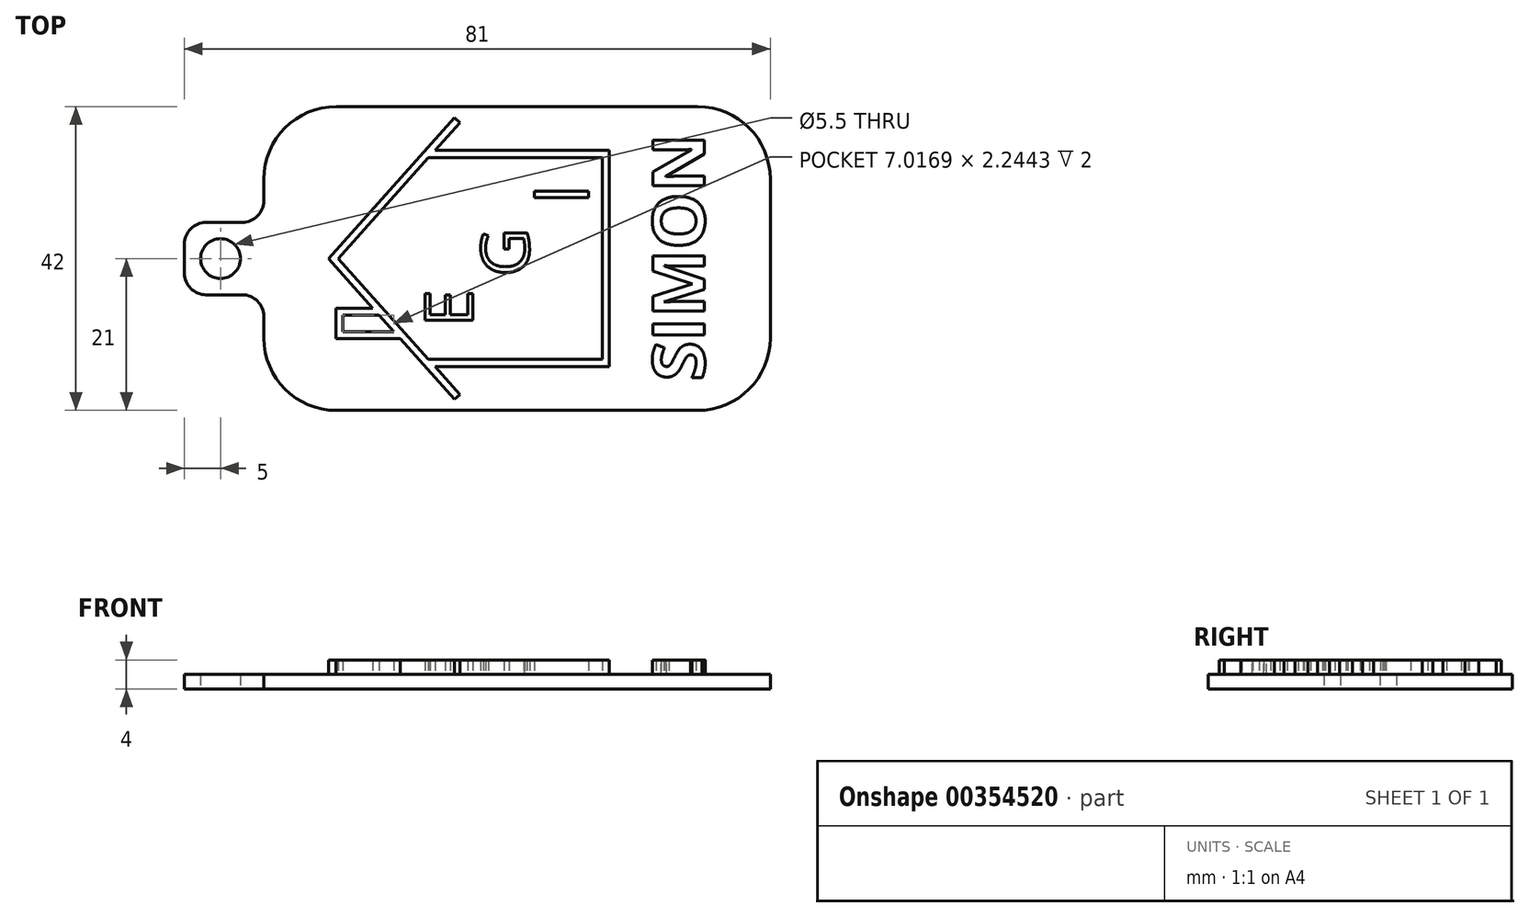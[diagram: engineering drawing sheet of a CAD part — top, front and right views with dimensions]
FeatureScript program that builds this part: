
annotation { "Feature Type Name" : "Feature", "Feature Type Description" : "" }
export const myFeature = defineFeature(function(context is Context, id is Id, definition is map)
    precondition{}
    {
        {
            var Q0;
            Q0=qCreatedBy(makeId("Top.planeOp"),FACE);
            var sketch = newSketch(context, id + "F0", { "sketchPlane" : qUnion([Q0])});
            skLineSegment(sketch, "E0.bottom", {"start": v(30, 21) * mm, "end": v(-20, 21) * mm});
            skLineSegment(sketch, "E0.top", {"start": v(30, -21) * mm, "end": v(-20, -21) * mm});
            skLineSegment(sketch, "E0.left", {"start": v(40, 11) * mm, "end": v(40, -11) * mm});
            skLineSegment(sketch, "E0.right", {"start": v(-30, 11) * mm, "end": v(-30, 8) * mm});
            skLineSegment(sketch, "E1.bottom", {"start": v(-38, 5) * mm, "end": v(-33, 5) * mm});
            skLineSegment(sketch, "E1.top", {"start": v(-38, -5) * mm, "end": v(-33, -5) * mm});
            skLineSegment(sketch, "E1.left", {"start": v(-41, 2) * mm, "end": v(-41, -2) * mm});
            skLineSegment(sketch, "E2.trimOffspring", {"start": v(-30, -8) * mm, "end": v(-30, -11) * mm});
            skPoint(sketch, "E3.visualSharp", {"position": v(-30, 5) * mm});
            skArc(sketch, "E3.filletArc", {"start": v(-33, 5) * mm, "mid": v(-30.88, 5.88) * mm, "end": v(-30, 8) * mm});
            skPoint(sketch, "E4.visualSharp", {"position": v(-41, 5) * mm});
            skArc(sketch, "E4.filletArc", {"start": v(-38, 5) * mm, "mid": v(-40.12, 4.12) * mm, "end": v(-41, 2) * mm});
            skPoint(sketch, "E5.visualSharp", {"position": v(-41, -5) * mm});
            skArc(sketch, "E5.filletArc", {"start": v(-41, -2) * mm, "mid": v(-40.12, -4.12) * mm, "end": v(-38, -5) * mm});
            skPoint(sketch, "E6.visualSharp", {"position": v(-30, -5) * mm});
            skArc(sketch, "E6.filletArc", {"start": v(-30, -8) * mm, "mid": v(-30.88, -5.88) * mm, "end": v(-33, -5) * mm});
            skPoint(sketch, "E7.visualSharp", {"position": v(-30, 21) * mm});
            skArc(sketch, "E7.filletArc", {"start": v(-20, 21) * mm, "mid": v(-27.07, 18.07) * mm, "end": v(-30, 11) * mm});
            skPoint(sketch, "E8.visualSharp", {"position": v(-30, -21) * mm});
            skArc(sketch, "E8.filletArc", {"start": v(-30, -11) * mm, "mid": v(-27.07, -18.07) * mm, "end": v(-20, -21) * mm});
            skPoint(sketch, "E9.visualSharp", {"position": v(40, 21) * mm});
            skArc(sketch, "E9.filletArc", {"start": v(40, 11) * mm, "mid": v(37.07, 18.07) * mm, "end": v(30, 21) * mm});
            skPoint(sketch, "E10.visualSharp", {"position": v(40, -21) * mm});
            skArc(sketch, "E10.filletArc", {"start": v(30, -21) * mm, "mid": v(37.07, -18.07) * mm, "end": v(40, -11) * mm});
            skCircle(sketch, "E11", {"center": v(-36, 0) * mm, "radius": 2.75 * mm});
            skPoint(sketch, "E11.centerSnap0", {"position": v(-41, 0) * mm});
            skSolve(sketch);
        }
        {
            var Q0;
            Q0=makeQuery(id+"F0.imprint","IMPRINT",FACE,{"disambiguationData":[TD([[makeQuery(id+"F0.imprint","IMPRINT",EDGE,{"derivedFrom":sQuery(id+"F0.wireOp",EDGE,"E0.bottom")}),1.0]])]});
            extrude(context, id + "F1", {"entities" : qUnion([Q0]), "depth" : 2 * mm});
        }
        {
            var Q0;
            Q0=makeQuery(id+"F1.opExtrude","CAP_FACE",FACE,{"disambiguationData":[OSD([sQuery(id+"F0.wireOp",EDGE,"E0.bottom"),sQuery(id+"F0.wireOp",EDGE,"E0.top"),sQuery(id+"F0.wireOp",EDGE,"E0.left"),sQuery(id+"F0.wireOp",EDGE,"E0.right"),sQuery(id+"F0.wireOp",EDGE,"E1.bottom"),sQuery(id+"F0.wireOp",EDGE,"E1.top"),sQuery(id+"F0.wireOp",EDGE,"E1.left"),sQuery(id+"F0.wireOp",EDGE,"E2.trimOffspring"),sQuery(id+"F0.wireOp",EDGE,"E3.filletArc"),sQuery(id+"F0.wireOp",EDGE,"E4.filletArc"),sQuery(id+"F0.wireOp",EDGE,"E5.filletArc"),sQuery(id+"F0.wireOp",EDGE,"E6.filletArc"),sQuery(id+"F0.wireOp",EDGE,"E7.filletArc"),sQuery(id+"F0.wireOp",EDGE,"E8.filletArc"),sQuery(id+"F0.wireOp",EDGE,"E9.filletArc"),sQuery(id+"F0.wireOp",EDGE,"E10.filletArc"),sQuery(id+"F0.wireOp",EDGE,"E11")])],"isStart":false});
            var sketch = newSketch(context, id + "F2", { "sketchPlane" : qUnion([Q0])});
            skLineSegment(sketch, "E12", {"start": v(-19.74, 0) * mm, "end": v(-7.25, -13.94) * mm});
            skLineSegment(sketch, "E13", {"start": v(-6.35, -14.94) * mm, "end": v(17.76, -14.94) * mm});
            skLineSegment(sketch, "E14", {"start": v(16.76, -13.94) * mm, "end": v(16.76, 0) * mm});
            skLineSegment(sketch, "E15.0", {"start": v(-21.08, 0) * mm, "end": v(-14.95, -6.84) * mm});
            skLineSegment(sketch, "E16.0", {"start": v(-7.25, -13.94) * mm, "end": v(16.76, -13.94) * mm});
            skLineSegment(sketch, "E17.0", {"start": v(17.76, -14.94) * mm, "end": v(17.76, 0) * mm});
            skLineSegment(sketch, "E18", {"start": v(-3.64, -19.47) * mm, "end": v(-2.9, -18.8) * mm});
            skLineSegment(sketch, "E19.trimOffspring", {"start": v(-6.35, -14.94) * mm, "end": v(-2.9, -18.8) * mm});
            skLineSegment(sketch, "E20", {"start": v(-14.06, -7.84) * mm, "end": v(-19.06, -7.84) * mm});
            skLineSegment(sketch, "E21.0", {"start": v(-11.15, -11.09) * mm, "end": v(-20.06, -11.09) * mm});
            skLineSegment(sketch, "E22.0", {"start": v(-46, 2) * mm, "end": v(-46, -2) * mm});
            skArc(sketch, "E22.1", {"start": v(-38, 10) * mm, "mid": v(-43.66, 7.66) * mm, "end": v(-46, 2) * mm});
            skLineSegment(sketch, "E22.2", {"start": v(-35, 10) * mm, "end": v(-38, 10) * mm});
            skLineSegment(sketch, "E22.3", {"start": v(-20, -26) * mm, "end": v(30, -26) * mm});
            skArc(sketch, "E22.4", {"start": v(-35, -11) * mm, "mid": v(-30.6, -21.6) * mm, "end": v(-20, -26) * mm});
            skLineSegment(sketch, "E22.5", {"start": v(-35, -10) * mm, "end": v(-35, -11) * mm});
            skLineSegment(sketch, "E22.6", {"start": v(-38, -10) * mm, "end": v(-35, -10) * mm});
            skArc(sketch, "E22.7", {"start": v(30, -26) * mm, "mid": v(40.6, -21.6) * mm, "end": v(45, -11) * mm});
            skLineSegment(sketch, "E22.8", {"start": v(45, -11) * mm, "end": v(45, 11) * mm});
            skArc(sketch, "E22.9", {"start": v(45, 11) * mm, "mid": v(40.6, 21.6) * mm, "end": v(30, 26) * mm});
            skArc(sketch, "E22.10", {"start": v(-46, -2) * mm, "mid": v(-43.66, -7.66) * mm, "end": v(-38, -10) * mm});
            skLineSegment(sketch, "E22.11", {"start": v(30, 26) * mm, "end": v(-20, 26) * mm});
            skArc(sketch, "E22.12", {"start": v(-20, 26) * mm, "mid": v(-30.6, 21.6) * mm, "end": v(-35, 11) * mm});
            skLineSegment(sketch, "E22.13", {"start": v(-35, 11) * mm, "end": v(-35, 10) * mm});
            skLineSegment(sketch, "E23", {"start": v(-19.06, -10.09) * mm, "end": v(-19.06, -7.84) * mm});
            skLineSegment(sketch, "E24.0", {"start": v(-20.06, -11.09) * mm, "end": v(-20.06, -6.84) * mm});
            skLineSegment(sketch, "E25.trimOffspring", {"start": v(-11.15, -11.09) * mm, "end": v(-3.64, -19.47) * mm});
            skLineSegment(sketch, "E26.trimOffspring", {"start": v(-12.04, -10.09) * mm, "end": v(-19.06, -10.09) * mm});
            skLineSegment(sketch, "E27.trimOffspring", {"start": v(-14.95, -6.84) * mm, "end": v(-20.06, -6.84) * mm});
            skLineSegment(sketch, "E28.trimOffspring", {"start": v(-14.06, -7.84) * mm, "end": v(-12.04, -10.09) * mm});
            skLineSegment(sketch, "E29", {"start": v(0, 0) * mm, "end": v(-30, 0) * mm, "construction": true});
            skLineSegment(sketch, "E30.MirrorCS", {"start": v(16.76, 13.94) * mm, "end": v(16.76, 0) * mm});
            skLineSegment(sketch, "E31.MirrorCS", {"start": v(17.76, 14.94) * mm, "end": v(17.76, 0) * mm});
            skLineSegment(sketch, "E32.MirrorCS", {"start": v(-6.35, 14.94) * mm, "end": v(17.76, 14.94) * mm});
            skLineSegment(sketch, "E33.MirrorCS", {"start": v(-7.25, 13.94) * mm, "end": v(16.76, 13.94) * mm});
            skLineSegment(sketch, "E34.MirrorCS", {"start": v(-6.35, 14.94) * mm, "end": v(-2.9, 18.8) * mm});
            skLineSegment(sketch, "E35.MirrorCS", {"start": v(-21.08, 0) * mm, "end": v(-3.64, 19.47) * mm});
            skLineSegment(sketch, "E36.MirrorCS", {"start": v(-3.64, 19.47) * mm, "end": v(-2.9, 18.8) * mm});
            skLineSegment(sketch, "E37.MirrorCS", {"start": v(-19.74, 0) * mm, "end": v(-7.25, 13.94) * mm});
            skPoint(sketch, "E38.orphan", {"position": v(-11.15, 11.09) * mm});
            skSolve(sketch);
        }
        {
            var Q0;
            Q0=makeQuery(id+"F2.imprint","IMPRINT",FACE,{"disambiguationData":[TD([[makeQuery(id+"F2.imprint","IMPRINT",EDGE,{"derivedFrom":sQuery(id+"F2.wireOp",EDGE,"E12")}),-1.0]])]});
            extrude(context, id + "F3", {"entities" : qUnion([Q0]), "operationType" : NewBodyOperationType.ADD, "depth" : 2 * mm});
        }
        {
            var Q0;
            Q0=makeQuery(id+"F3.boolean.opBoolean","SPLIT",FACE,{"disambiguationData":[TD([makeQuery(id+"F3.opExtrude","SWEPT_FACE",FACE,{"disambiguationData":[OSD([sQuery(id+"F2.wireOp",EDGE,"E12")])]})])],"derivedFrom":makeQuery(id+"F1.opExtrude","CAP_FACE",FACE,{"disambiguationData":[OSD([sQuery(id+"F0.wireOp",EDGE,"E0.bottom"),sQuery(id+"F0.wireOp",EDGE,"E0.top"),sQuery(id+"F0.wireOp",EDGE,"E0.left"),sQuery(id+"F0.wireOp",EDGE,"E0.right"),sQuery(id+"F0.wireOp",EDGE,"E1.bottom"),sQuery(id+"F0.wireOp",EDGE,"E1.top"),sQuery(id+"F0.wireOp",EDGE,"E1.left"),sQuery(id+"F0.wireOp",EDGE,"E2.trimOffspring"),sQuery(id+"F0.wireOp",EDGE,"E3.filletArc"),sQuery(id+"F0.wireOp",EDGE,"E4.filletArc"),sQuery(id+"F0.wireOp",EDGE,"E5.filletArc"),sQuery(id+"F0.wireOp",EDGE,"E6.filletArc"),sQuery(id+"F0.wireOp",EDGE,"E7.filletArc"),sQuery(id+"F0.wireOp",EDGE,"E8.filletArc"),sQuery(id+"F0.wireOp",EDGE,"E9.filletArc"),sQuery(id+"F0.wireOp",EDGE,"E10.filletArc"),sQuery(id+"F0.wireOp",EDGE,"E11")])],"isStart":false})});
            var sketch = newSketch(context, id + "F4", { "sketchPlane" : qUnion([Q0])});
            skText(sketch, "E39", { "text": "E", "fontName": "OpenSans-Regular.ttf"});
            const initialGuessF4  = {"E39": [-0.0011, -0.00945, 0, 1, 0.00667]};
            skSetInitialGuess(sketch, initialGuessF4);
            skSolve(sketch);
        }
        {
            var Q0;
            Q0=makeQuery(id+"F4.imprint","IMPRINT",FACE,{"disambiguationData":[TD([[makeQuery(id+"F4.imprint","IMPRINT",EDGE,{"derivedFrom":sQuery(id+"F4.wireOp",EDGE,"E39.sketch_text.stroke-0")}),-1.0]])]});
            extrude(context, id + "F5", {"entities" : qUnion([Q0]), "operationType" : NewBodyOperationType.ADD, "depth" : 2 * mm});
        }
        {
            var Q0;
            Q0=makeQuery(id+"F3.boolean.opBoolean","SPLIT",FACE,{"disambiguationData":[TD([makeQuery(id+"F3.opExtrude","SWEPT_FACE",FACE,{"disambiguationData":[OSD([sQuery(id+"F2.wireOp",EDGE,"E12")])]})])],"derivedFrom":makeQuery(id+"F1.opExtrude","CAP_FACE",FACE,{"disambiguationData":[OSD([sQuery(id+"F0.wireOp",EDGE,"E0.bottom"),sQuery(id+"F0.wireOp",EDGE,"E0.top"),sQuery(id+"F0.wireOp",EDGE,"E0.left"),sQuery(id+"F0.wireOp",EDGE,"E0.right"),sQuery(id+"F0.wireOp",EDGE,"E1.bottom"),sQuery(id+"F0.wireOp",EDGE,"E1.top"),sQuery(id+"F0.wireOp",EDGE,"E1.left"),sQuery(id+"F0.wireOp",EDGE,"E2.trimOffspring"),sQuery(id+"F0.wireOp",EDGE,"E3.filletArc"),sQuery(id+"F0.wireOp",EDGE,"E4.filletArc"),sQuery(id+"F0.wireOp",EDGE,"E5.filletArc"),sQuery(id+"F0.wireOp",EDGE,"E6.filletArc"),sQuery(id+"F0.wireOp",EDGE,"E7.filletArc"),sQuery(id+"F0.wireOp",EDGE,"E8.filletArc"),sQuery(id+"F0.wireOp",EDGE,"E9.filletArc"),sQuery(id+"F0.wireOp",EDGE,"E10.filletArc"),sQuery(id+"F0.wireOp",EDGE,"E11")])],"isStart":false})});
            var sketch = newSketch(context, id + "F6", { "sketchPlane" : qUnion([Q0])});
            skText(sketch, "E40", { "text": "G", "fontName": "OpenSans-Regular.ttf"});
            skPoint(sketch, "E41", {"position": v(-7.03, -6.3) * mm});
            const initialGuessF6  = {"E40": [0.00664, -0.0025, 0, 1, 0.00664]};
            skSetInitialGuess(sketch, initialGuessF6);
            skSolve(sketch);
        }
        {
            var Q0;
            Q0 = qSketchRegion(id + "F6", true);
            extrude(context, id + "F7", {"entities" : qUnion([Q0]), "operationType" : NewBodyOperationType.ADD, "depth" : 2 * mm});
        }
        {
            var Q0;
            Q0=makeQuery(id+"F3.boolean.opBoolean","SPLIT",FACE,{"disambiguationData":[TD([makeQuery(id+"F3.opExtrude","SWEPT_FACE",FACE,{"disambiguationData":[OSD([sQuery(id+"F2.wireOp",EDGE,"E12")])]})])],"derivedFrom":makeQuery(id+"F1.opExtrude","CAP_FACE",FACE,{"disambiguationData":[OSD([sQuery(id+"F0.wireOp",EDGE,"E0.bottom"),sQuery(id+"F0.wireOp",EDGE,"E0.top"),sQuery(id+"F0.wireOp",EDGE,"E0.left"),sQuery(id+"F0.wireOp",EDGE,"E0.right"),sQuery(id+"F0.wireOp",EDGE,"E1.bottom"),sQuery(id+"F0.wireOp",EDGE,"E1.top"),sQuery(id+"F0.wireOp",EDGE,"E1.left"),sQuery(id+"F0.wireOp",EDGE,"E2.trimOffspring"),sQuery(id+"F0.wireOp",EDGE,"E3.filletArc"),sQuery(id+"F0.wireOp",EDGE,"E4.filletArc"),sQuery(id+"F0.wireOp",EDGE,"E5.filletArc"),sQuery(id+"F0.wireOp",EDGE,"E6.filletArc"),sQuery(id+"F0.wireOp",EDGE,"E7.filletArc"),sQuery(id+"F0.wireOp",EDGE,"E8.filletArc"),sQuery(id+"F0.wireOp",EDGE,"E9.filletArc"),sQuery(id+"F0.wireOp",EDGE,"E10.filletArc"),sQuery(id+"F0.wireOp",EDGE,"E11")])],"isStart":false})});
            var sketch = newSketch(context, id + "F8", { "sketchPlane" : qUnion([Q0])});
            skText(sketch, "E42", { "text": "I", "fontName": "OpenSans-Regular.ttf"});
            const initialGuessF8  = {"E42": [0.01488, 0.0074, 0, 1, 0.00758]};
            skSetInitialGuess(sketch, initialGuessF8);
            skSolve(sketch);
        }
        {
            var Q0;
            Q0=makeQuery(id+"F8.imprint","IMPRINT",FACE,{"disambiguationData":[TD([[makeQuery(id+"F8.imprint","IMPRINT",EDGE,{"derivedFrom":sQuery(id+"F8.wireOp",EDGE,"E42.sketch_text.stroke-0")}),-1.0]])]});
            extrude(context, id + "F9", {"entities" : qUnion([Q0]), "operationType" : NewBodyOperationType.ADD, "depth" : 2 * mm});
        }
        {
            var Q0;
            {var subQ0=sQuery(id+"F0.wireOp",EDGE,"E11");var subQ1=sQuery(id+"F0.wireOp",EDGE,"E10.filletArc");var subQ2=sQuery(id+"F0.wireOp",EDGE,"E9.filletArc");var subQ3=sQuery(id+"F0.wireOp",EDGE,"E8.filletArc");var subQ4=sQuery(id+"F0.wireOp",EDGE,"E7.filletArc");var subQ5=sQuery(id+"F0.wireOp",EDGE,"E6.filletArc");var subQ6=sQuery(id+"F0.wireOp",EDGE,"E5.filletArc");var subQ7=sQuery(id+"F0.wireOp",EDGE,"E0.left");var subQ8=sQuery(id+"F0.wireOp",EDGE,"E0.top");var subQ9=sQuery(id+"F0.wireOp",EDGE,"E0.right");var subQ10=sQuery(id+"F0.wireOp",EDGE,"E0.bottom");var subQ11=sQuery(id+"F0.wireOp",EDGE,"E4.filletArc");var subQ12=sQuery(id+"F0.wireOp",EDGE,"E1.bottom");var subQ13=sQuery(id+"F0.wireOp",EDGE,"E1.top");var subQ14=sQuery(id+"F0.wireOp",EDGE,"E1.left");var subQ15=sQuery(id+"F0.wireOp",EDGE,"E2.trimOffspring");var subQ16=sQuery(id+"F0.wireOp",EDGE,"E3.filletArc");Q0=makeQuery(id+"F3.boolean.opBoolean","SPLIT",FACE,{"disambiguationData":[TD([makeQuery(id+"F1.opExtrude","SWEPT_FACE",FACE,{"disambiguationData":[OSD([subQ10])]})])],"derivedFrom":makeQuery(id+"F1.opExtrude","CAP_FACE",FACE,{"disambiguationData":[OSD([subQ10,subQ8,subQ7,subQ9,subQ12,subQ13,subQ14,subQ15,subQ16,subQ11,subQ6,subQ5,subQ4,subQ3,subQ2,subQ1,subQ0])],"isStart":false})});}
            var sketch = newSketch(context, id + "F10", { "sketchPlane" : qUnion([Q0])});
            skText(sketch, "E43", { "text": "SIMON", "fontName": "OpenSans-Bold.ttf"});
            skPoint(sketch, "E43.secondSnap0", {"position": v(-18.02, -3.42) * mm});
            const initialGuessF10  = {"E43": [0.0309, -0.01693, 0, 1, 0.00717]};
            skSetInitialGuess(sketch, initialGuessF10);
            skSolve(sketch);
        }
        {
            var Q0;
            Q0 = qSketchRegion(id + "F10", true);
            extrude(context, id + "F11", {"entities" : qUnion([Q0]), "operationType" : NewBodyOperationType.ADD, "depth" : 2 * mm});
        }
    });
